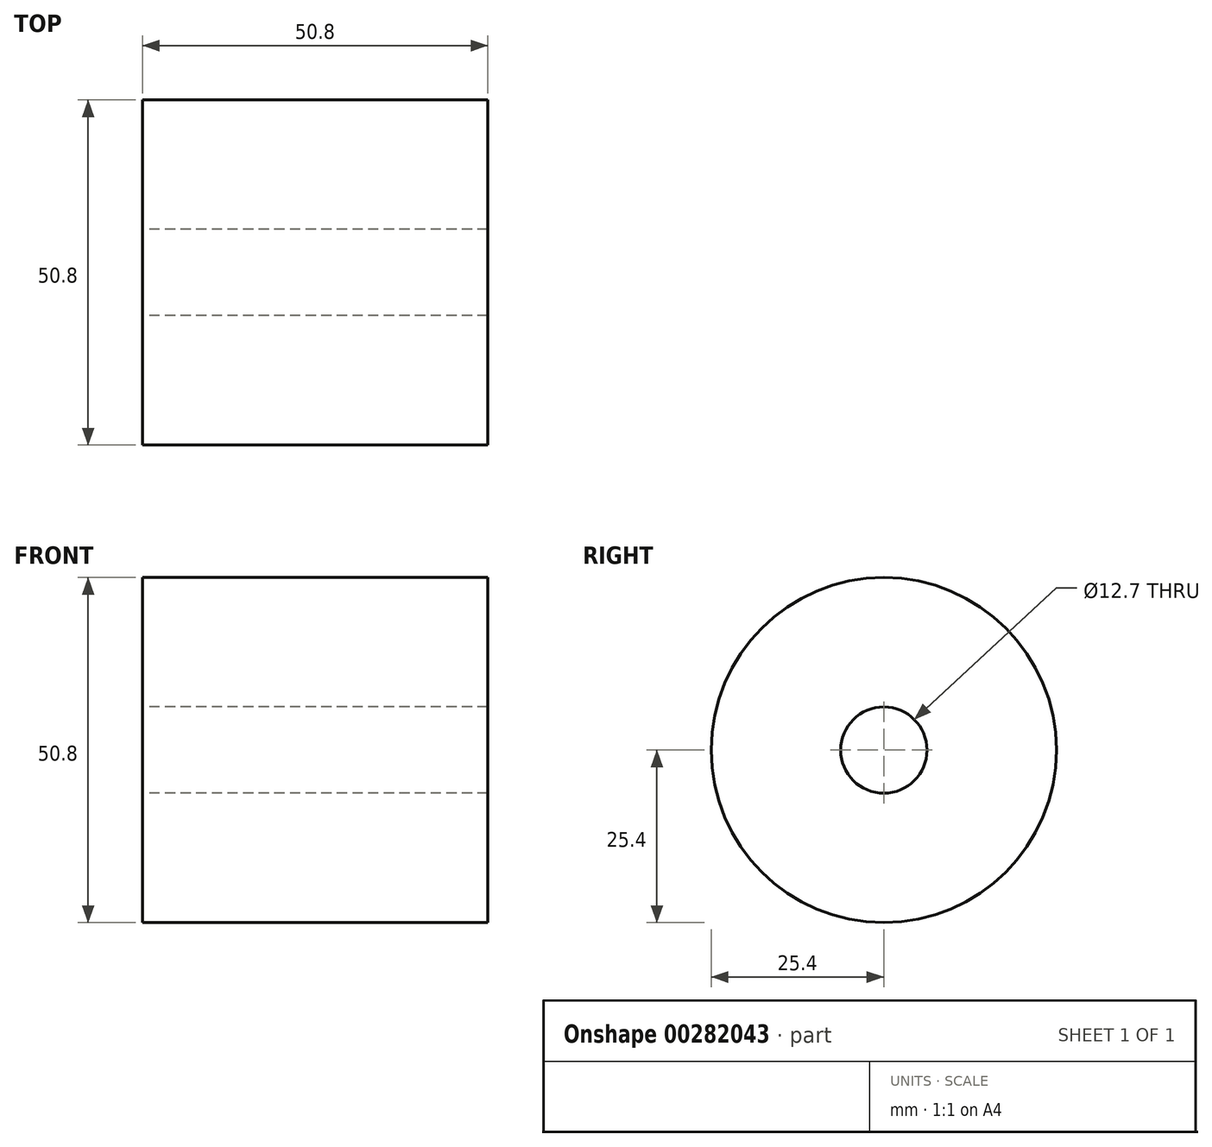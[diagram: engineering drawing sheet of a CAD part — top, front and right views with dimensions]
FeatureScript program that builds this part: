
annotation { "Feature Type Name" : "Feature", "Feature Type Description" : "" }
export const myFeature = defineFeature(function(context is Context, id is Id, definition is map)
    precondition{}
    {
        {
            var Q0;
            Q0=qCreatedBy(makeId("Right.planeOp"),FACE);
            var sketch = newSketch(context, id + "F0", { "sketchPlane" : qUnion([Q0])});
            skCircle(sketch, "E0", {"center": v(0, 0) * mm, "radius": 25.4 * mm});
            skCircle(sketch, "E1", {"center": v(0, 0) * mm, "radius": 6.35 * mm});
            skSolve(sketch);
        }
        {
            var Q0;
            Q0 = qSketchRegion(id + "F0", true);
            extrude(context, id + "F1", {"entities" : qUnion([Q0]), "depth" : 50.8 * mm});
        }
    });
